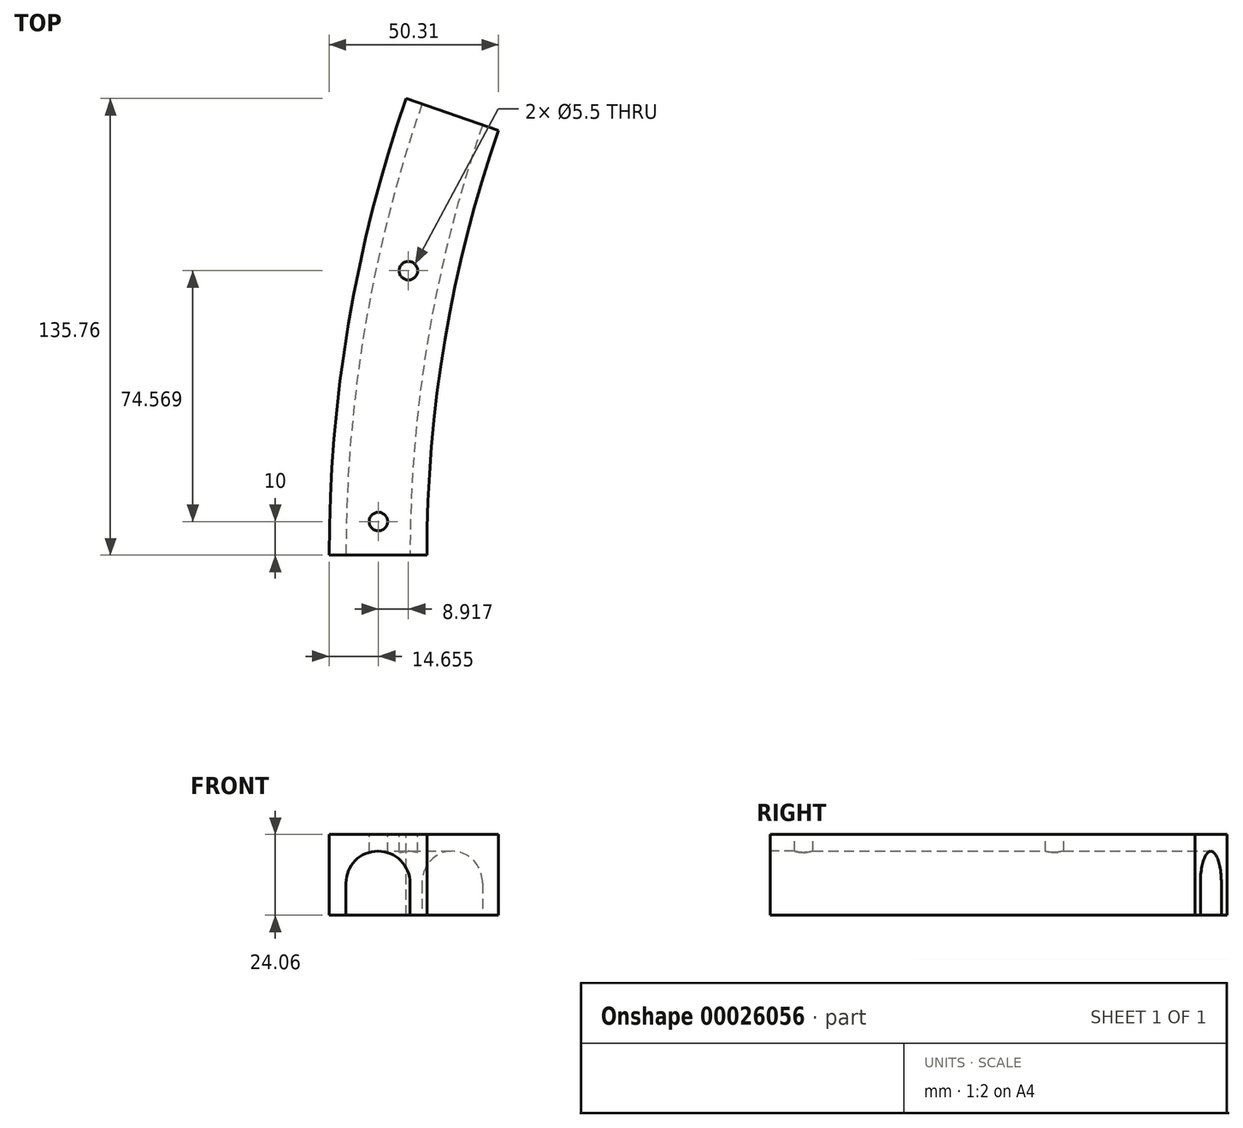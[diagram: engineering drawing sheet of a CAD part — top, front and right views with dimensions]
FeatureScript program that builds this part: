
annotation { "Feature Type Name" : "Feature", "Feature Type Description" : "" }
export const myFeature = defineFeature(function(context is Context, id is Id, definition is map)
    precondition{}
    {
        {
            var Q0;
            Q0=qCreatedBy(makeId("Top.planeOp"),FACE);
            var sketch = newSketch(context, id + "F0", { "sketchPlane" : qUnion([Q0])});
            skCircle(sketch, "E0", {"center": v(0, 0) * mm, "radius": 400 * mm, "construction": true});
            skArc(sketch, "E1", {"start": v(-377.94, 131) * mm, "mid": v(-394.45, 66.42) * mm, "end": v(-400, 0) * mm});
            skSolve(sketch);
        }
        {
            var Q0;
            Q0=qCreatedBy(makeId("Front.planeOp"),FACE);
            var sketch = newSketch(context, id + "F1", { "sketchPlane" : qUnion([Q0])});
            skLineSegment(sketch, "E2.bottom", {"start": v(-385.47, -9.52) * mm, "end": v(-390.47, -9.52) * mm});
            skLineSegment(sketch, "E2.top", {"start": v(-385.47, 14.53) * mm, "end": v(-414.52, 14.53) * mm});
            skLineSegment(sketch, "E2.left", {"start": v(-385.47, -9.53) * mm, "end": v(-385.47, 14.53) * mm});
            skLineSegment(sketch, "E2.right", {"start": v(-414.52, -9.53) * mm, "end": v(-414.52, 14.53) * mm});
            skArc(sketch, "E3", {"start": v(-390.47, 0) * mm, "mid": v(-400, 9.53) * mm, "end": v(-409.52, 0) * mm});
            skLineSegment(sketch, "E4", {"start": v(-409.52, 0) * mm, "end": v(-409.52, -9.53) * mm});
            skLineSegment(sketch, "E5", {"start": v(-390.47, 0) * mm, "end": v(-390.47, -9.53) * mm});
            skLineSegment(sketch, "E6", {"start": v(-390.47, 0) * mm, "end": v(-385.47, 0) * mm, "construction": true});
            skLineSegment(sketch, "E7", {"start": v(-409.52, 0) * mm, "end": v(-414.52, 0) * mm, "construction": true});
            skLineSegment(sketch, "E8", {"start": v(-400, 14.53) * mm, "end": v(-400, 9.53) * mm, "construction": true});
            skLineSegment(sketch, "E9.trimOffspring", {"start": v(-409.52, -9.53) * mm, "end": v(-414.52, -9.53) * mm});
            skSolve(sketch);
        }
        {
            var Q0;
            Q0=makeQuery(id+"F1.imprint","IMPRINT",FACE,{"disambiguationData":[TD([[makeQuery(id+"F1.imprint","IMPRINT",EDGE,{"derivedFrom":sQuery(id+"F1.wireOp",EDGE,"E2.bottom")}),-1.0]])]});
            var Q1;
            Q1=sQuery(id+"F0.wireOp",EDGE,"E1");
            sweep(context, id + "F2", {"profiles" : qUnion([Q0]), "path" : qUnion([Q1])});
        }
        {
            var Q0;
            Q0=makeQuery(id+"F2.opSweep","SWEPT_FACE",FACE,{"disambiguationData":[OSD([sQuery(id+"F0.wireOp",EDGE,"E1"),sQuery(id+"F1.wireOp",EDGE,"E2.top")])]});
            var sketch = newSketch(context, id + "F3", { "sketchPlane" : qUnion([Q0])});
            skCircle(sketch, "E10.0", {"center": v(0, 0) * mm, "radius": 400 * mm, "construction": true});
            skCircle(sketch, "E11", {"center": v(-399.87, 10) * mm, "radius": 2.75 * mm});
            skCircle(sketch, "E12", {"center": v(-390.96, 84.57) * mm, "radius": 2.75 * mm});
            skLineSegment(sketch, "E13", {"start": v(-390.96, 84.57) * mm, "end": v(-399.87, 10) * mm, "construction": true});
            skSolve(sketch);
        }
        {
            var Q0;
            Q0 = qSketchRegion(id + "F3", true);
            extrude(context, id + "F4", {"entities" : qUnion([Q0]), "operationType" : NewBodyOperationType.REMOVE, "endBound" : BoundingType.THROUGH_ALL, "oppositeDirection" : true, "depth" : 25 * mm});
        }
    });
